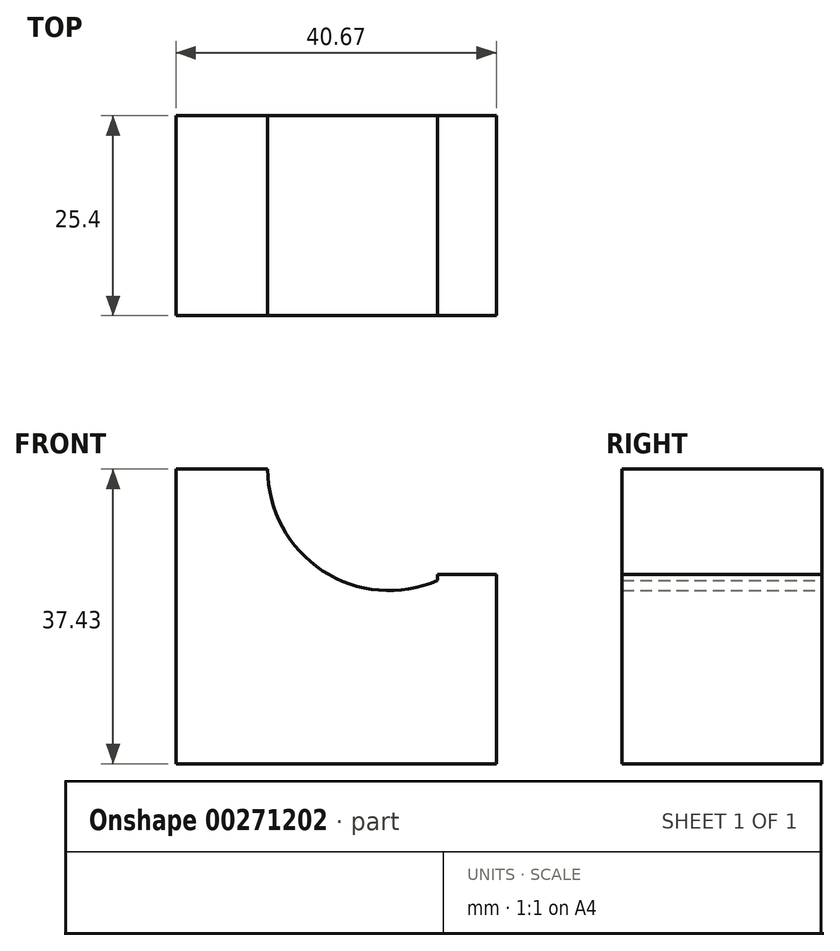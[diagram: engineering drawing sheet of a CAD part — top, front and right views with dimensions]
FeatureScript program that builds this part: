
annotation { "Feature Type Name" : "Feature", "Feature Type Description" : "" }
export const myFeature = defineFeature(function(context is Context, id is Id, definition is map)
    precondition{}
    {
        {
            var Q0;
            Q0=qCreatedBy(makeId("Front.planeOp"),FACE);
            var sketch = newSketch(context, id + "F0", { "sketchPlane" : qUnion([Q0])});
            skLineSegment(sketch, "E0", {"start": v(0, 0) * mm, "end": v(0, 24.06) * mm});
            skLineSegment(sketch, "E1", {"start": v(0, 24.06) * mm, "end": v(-7.44, 24.06) * mm});
            skLineSegment(sketch, "E2", {"start": v(-7.44, 24.06) * mm, "end": v(-7.44, 0) * mm});
            skLineSegment(sketch, "E3", {"start": v(-7.44, 0) * mm, "end": v(0, 0) * mm});
            skLineSegment(sketch, "E4", {"start": v(-29.02, 0) * mm, "end": v(-29.02, 37.43) * mm});
            skLineSegment(sketch, "E5", {"start": v(-29.02, 37.43) * mm, "end": v(-40.67, 37.43) * mm});
            skLineSegment(sketch, "E6", {"start": v(-40.67, 37.43) * mm, "end": v(-40.67, 0) * mm});
            skLineSegment(sketch, "E7", {"start": v(-40.67, 0) * mm, "end": v(-27.11, 0) * mm});
            skArc(sketch, "E8", {"start": v(-29.02, 37.43) * mm, "mid": v(-21.33, 24.08) * mm, "end": v(-5.92, 24.06) * mm});
            skLineSegment(sketch, "E9", {"start": v(-27.11, 0) * mm, "end": v(-5.92, 0) * mm});
            skSolve(sketch);
        }
        {
            var Q0;
            Q0 = qSketchRegion(id + "F0", true);
            extrude(context, id + "F1", {"entities" : qUnion([Q0]), "depth" : 25.4 * mm});
        }
    });
